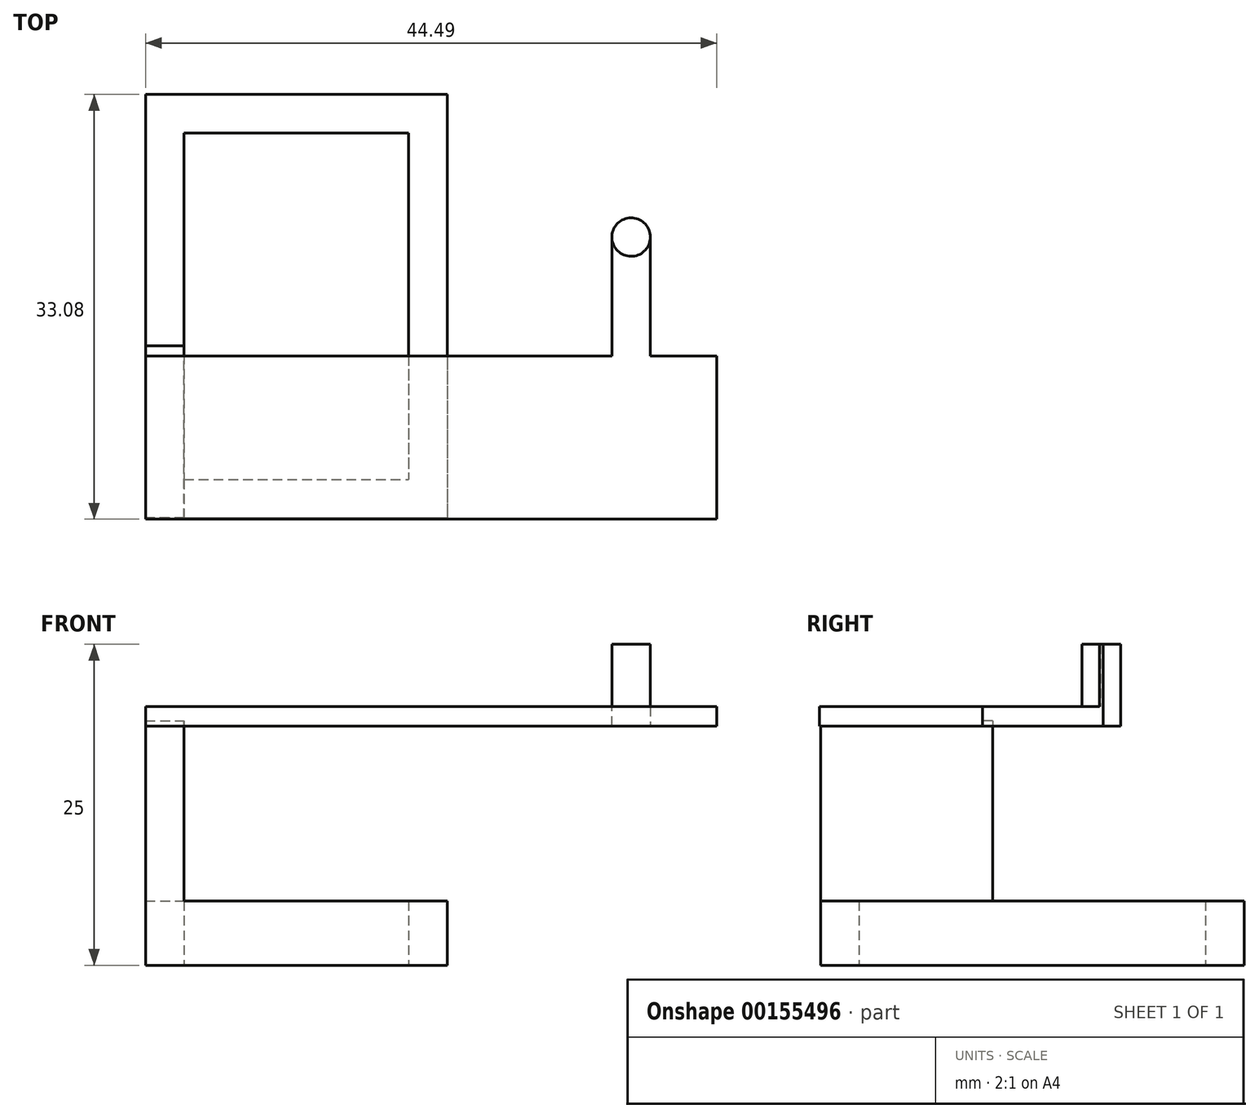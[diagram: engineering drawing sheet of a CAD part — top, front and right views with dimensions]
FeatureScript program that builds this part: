
annotation { "Feature Type Name" : "Feature", "Feature Type Description" : "" }
export const myFeature = defineFeature(function(context is Context, id is Id, definition is map)
    precondition{}
    {
        {
            var Q0;
            Q0=qCreatedBy(makeId("Top.planeOp"),FACE);
            var sketch = newSketch(context, id + "F0", { "sketchPlane" : qUnion([Q0])});
            skLineSegment(sketch, "E0.bottom", {"start": v(-34.24, 6.94) * mm, "end": v(-16.74, 6.94) * mm});
            skLineSegment(sketch, "E0.top", {"start": v(-34.24, -20.06) * mm, "end": v(-16.74, -20.06) * mm});
            skLineSegment(sketch, "E0.left", {"start": v(-34.24, 6.94) * mm, "end": v(-34.24, -20.06) * mm});
            skLineSegment(sketch, "E0.right", {"start": v(-16.74, 6.94) * mm, "end": v(-16.74, -20.06) * mm});
            skLineSegment(sketch, "E1.bottom", {"start": v(-37.24, 9.94) * mm, "end": v(-13.74, 9.94) * mm});
            skLineSegment(sketch, "E1.top", {"start": v(-37.24, -23.06) * mm, "end": v(-13.74, -23.06) * mm});
            skLineSegment(sketch, "E1.left", {"start": v(-37.24, 9.94) * mm, "end": v(-37.24, -23.06) * mm});
            skLineSegment(sketch, "E1.right", {"start": v(-13.74, 9.94) * mm, "end": v(-13.74, -23.06) * mm});
            skLineSegment(sketch, "E2", {"start": v(-34.24, 6.94) * mm, "end": v(-34.24, 9.94) * mm});
            skLineSegment(sketch, "E3", {"start": v(-34.24, -20.06) * mm, "end": v(-34.24, -23.06) * mm});
            skCircle(sketch, "E4", {"center": v(0.58, -1.17) * mm, "radius": 1.5 * mm});
            skLineSegment(sketch, "E5", {"start": v(2.08, -23.06) * mm, "end": v(-0.91, -23.06) * mm});
            skLineSegment(sketch, "E6", {"start": v(2.08, -8.4) * mm, "end": v(2.08, -1.03) * mm});
            skLineSegment(sketch, "E7", {"start": v(-0.91, -8.4) * mm, "end": v(-0.91, -1.08) * mm});
            skPoint(sketch, "E8.orphan", {"position": v(0, -2.55) * mm});
            skPoint(sketch, "E9.orphan", {"position": v(1.5, -2.55) * mm});
            skPoint(sketch, "E10.orphan", {"position": v(0, -23.06) * mm});
            skLineSegment(sketch, "E11", {"start": v(-37.24, -9.65) * mm, "end": v(-34.24, -9.65) * mm});
            skLineSegment(sketch, "E12", {"start": v(-0.91, -1.08) * mm, "end": v(-0.91, -23.06) * mm});
            skLineSegment(sketch, "E13", {"start": v(2.08, -1.03) * mm, "end": v(2.08, -23.06) * mm});
            skSolve(sketch);
        }
        {
            var Q0;
            Q0=makeQuery(id+"F0.imprint","IMPRINT",FACE,{"disambiguationData":[TD([[makeQuery(id+"F0.imprint","IMPRINT",EDGE,{"derivedFrom":sQuery(id+"F0.wireOp",EDGE,"E0.bottom")}),1.0]])]});
            extrude(context, id + "F1", {"entities" : qUnion([Q0]), "depth" : 5 * mm});
        }
        {
            var Q0;
            {var subQ0=sQuery(id+"F0.wireOp",EDGE,"E3");Q0=makeQuery(id+"F0.imprint","IMPRINT",FACE,{"disambiguationData":[TD([[makeQuery(id+"F0.imprint","IMPRINT",EDGE,{"derivedFrom":subQ0}),-1.0]])]});}
            extrude(context, id + "F2", {"entities" : qUnion([Q0]), "operationType" : NewBodyOperationType.ADD, "depth" : 19.05 * mm});
        }
        {
            var Q0;
            {var subQ0=sQuery(id+"F0.wireOp",EDGE,"E2");Q0=makeQuery(id+"F0.imprint","IMPRINT",FACE,{"disambiguationData":[TD([[makeQuery(id+"F0.imprint","IMPRINT",EDGE,{"derivedFrom":subQ0}),1.0]])]});}
            extrude(context, id + "F3", {"entities" : qUnion([Q0]), "operationType" : NewBodyOperationType.ADD, "depth" : 5 * mm});
        }
        {
            var Q0;
            Q0=qCreatedBy(makeId("Right.planeOp"),FACE);
            var sketch = newSketch(context, id + "F4", { "sketchPlane" : qUnion([Q0])});
            skLineSegment(sketch, "E14", {"start": v(-23.14, 18.63) * mm, "end": v(-10.44, 18.63) * mm});
            skLineSegment(sketch, "E15", {"start": v(-10.44, 18.63) * mm, "end": v(-10.44, 20.13) * mm});
            skLineSegment(sketch, "E16", {"start": v(-10.44, 20.13) * mm, "end": v(-23.14, 20.13) * mm});
            skLineSegment(sketch, "E17", {"start": v(-23.14, 20.13) * mm, "end": v(-23.14, 18.63) * mm});
            skSolve(sketch);
        }
        {
            var Q0;
            Q0=makeQuery(id+"F4.imprint","IMPRINT",FACE,{"disambiguationData":[TD([[makeQuery(id+"F4.imprint","IMPRINT",EDGE,{"derivedFrom":sQuery(id+"F4.wireOp",EDGE,"E14")}),1.0]])]});
            var Q1;
            {var subQ0=sQuery(id+"F0.wireOp",EDGE,"E1.left");Q1=makeQuery(id+"F3.boolean.opBoolean","MERGE",FACE,{"derivedFrom":[makeQuery(id+"F2.opExtrude","SWEPT_FACE",FACE,{"disambiguationData":[OSD([subQ0])]}),makeQuery(id+"F3.opExtrude","SWEPT_FACE",FACE,{"disambiguationData":[OSD([subQ0])]})]});}
            extrude(context, id + "F5", {"entities" : qUnion([Q0]), "operationType" : NewBodyOperationType.ADD, "endBound" : BoundingType.UP_TO_SURFACE, "oppositeDirection" : true, "endBoundEntityFace" : qUnion([Q1]), "depth" : 38.1 * mm, "hasSecondDirection" : true, "secondDirectionOppositeDirection" : false, "secondDirectionDepth" : 7.25 * mm});
        }
        {
            var Q0;
            Q0=makeQuery(id+"F0.imprint","IMPRINT",FACE,{"disambiguationData":[TD([[makeQuery(id+"F0.imprint","IMPRINT",EDGE,{"derivedFrom":sQuery(id+"F0.wireOp",EDGE,"E5")}),-1.0]])]});
            var Q1;
            Q1=makeQuery(id+"F5.opExtrude","SWEPT_FACE",FACE,{"disambiguationData":[OSD([sQuery(id+"F4.wireOp",EDGE,"E16")])]});
            var Q2;
            Q2=makeQuery(id+"F5.opExtrude","SWEPT_FACE",FACE,{"disambiguationData":[OSD([sQuery(id+"F4.wireOp",EDGE,"E14")])]});
            extrude(context, id + "F6", {"entities" : qUnion([Q0]), "operationType" : NewBodyOperationType.ADD, "endBound" : BoundingType.UP_TO_SURFACE, "endBoundEntityFace" : qUnion([Q1]), "depth" : 25 * mm, "hasSecondDirection" : true, "secondDirectionBound" : SecondDirectionBoundingType.UP_TO_SURFACE, "secondDirectionOppositeDirection" : false, "secondDirectionBoundEntityFace" : qUnion([Q2]), "secondDirectionDepth" : 25 * mm});
        }
        {
            var Q0;
            {var subQ0=sQuery(id+"F0.wireOp",EDGE,"E6");Q0=makeQuery(id+"F0.imprint","IMPRINT",FACE,{"disambiguationData":[TD([[makeQuery(id+"F0.imprint","IMPRINT",EDGE,{"derivedFrom":subQ0}),1.0]])]});}
            var Q1;
            {var subQ0=sQuery(id+"F0.wireOp",EDGE,"E12");var subQ1=sQuery(id+"F0.wireOp",EDGE,"E4");var subQ2=makeQuery(id+"F0.imprint","INTERSECT",VERTEX,{"disambiguationData":[OD(0.0)],"derivedFrom":[subQ1,subQ0]});Q1=makeQuery(id+"F0.imprint","IMPRINT",FACE,{"disambiguationData":[TD([[makeQuery(id+"F0.imprint","IMPRINT",EDGE,{"disambiguationData":[TD([[subQ2,1.0]])],"derivedFrom":subQ1}),1.0]])]});}
            var Q2;
            Q2=makeQuery(id+"F5.opExtrude","SWEPT_FACE",FACE,{"disambiguationData":[OSD([sQuery(id+"F4.wireOp",EDGE,"E14")])]});
            extrude(context, id + "F7", {"entities" : qUnion([Q0, Q1]), "operationType" : NewBodyOperationType.ADD, "depth" : 25 * mm, "hasSecondDirection" : true, "secondDirectionBound" : SecondDirectionBoundingType.UP_TO_SURFACE, "secondDirectionOppositeDirection" : false, "secondDirectionBoundEntityFace" : qUnion([Q2]), "secondDirectionDepth" : 25 * mm});
        }
    });
